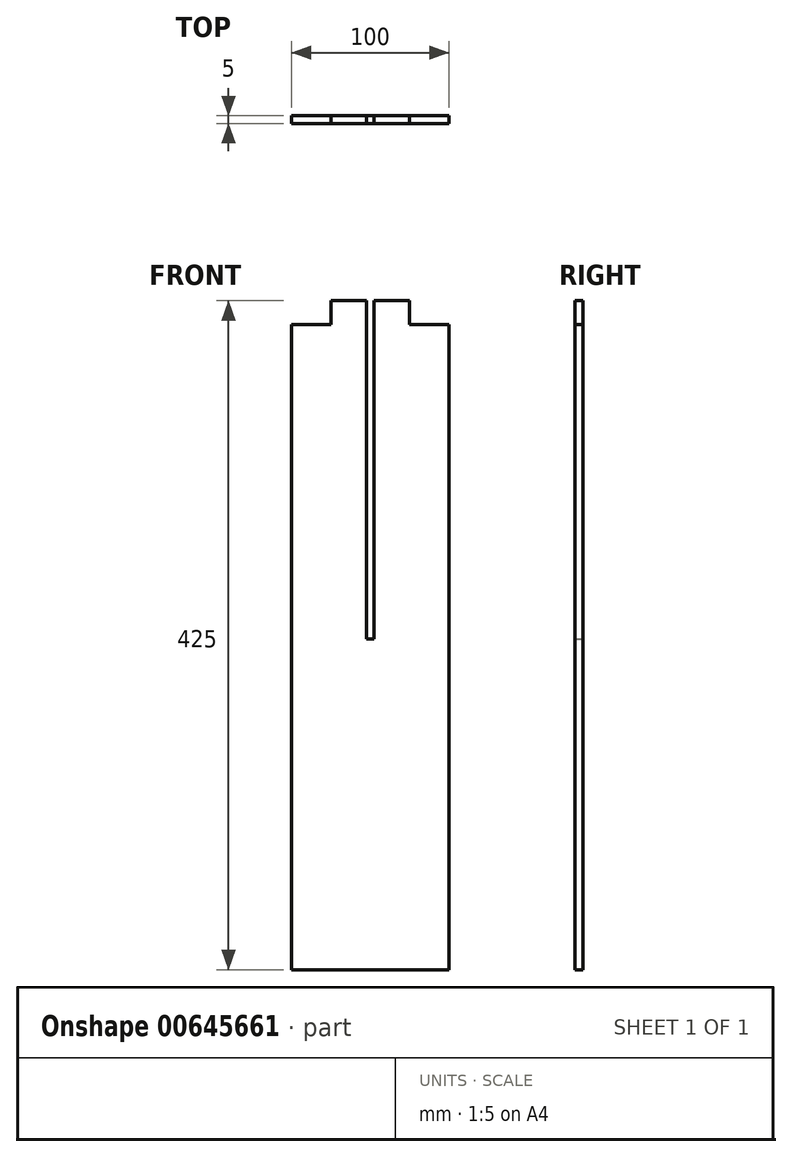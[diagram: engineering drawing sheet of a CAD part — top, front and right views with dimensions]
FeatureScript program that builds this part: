
annotation { "Feature Type Name" : "Feature", "Feature Type Description" : "" }
export const myFeature = defineFeature(function(context is Context, id is Id, definition is map)
    precondition{}
    {
        {
            var Q0;
            Q0=qCreatedBy(makeId("Front.planeOp"),FACE);
            var sketch = newSketch(context, id + "F0", { "sketchPlane" : qUnion([Q0])});
            skLineSegment(sketch, "E0.bottom", {"start": v(0, 0) * mm, "end": v(-100, 0) * mm});
            skLineSegment(sketch, "E0.left", {"start": v(0, 0) * mm, "end": v(0, 410) * mm});
            skLineSegment(sketch, "E0.right", {"start": v(-100, 0) * mm, "end": v(-100, 410) * mm});
            skLineSegment(sketch, "E1", {"start": v(-100, 410) * mm, "end": v(-75, 410) * mm});
            skLineSegment(sketch, "E2", {"start": v(-25, 410) * mm, "end": v(0, 410) * mm});
            skLineSegment(sketch, "E3.left", {"start": v(-52.5, 410) * mm, "end": v(-52.5, 410) * mm});
            skLineSegment(sketch, "E3.right", {"start": v(-47.5, 410) * mm, "end": v(-47.5, 410) * mm});
            skLineSegment(sketch, "E4.bottom", {"start": v(-52.5, 210) * mm, "end": v(-47.5, 210) * mm});
            skLineSegment(sketch, "E4.left", {"start": v(-52.5, 210) * mm, "end": v(-52.5, 410) * mm});
            skLineSegment(sketch, "E4.right", {"start": v(-47.5, 210) * mm, "end": v(-47.5, 410) * mm});
            skLineSegment(sketch, "E5.top", {"start": v(-47.5, 425) * mm, "end": v(-25, 425) * mm});
            skLineSegment(sketch, "E5.left", {"start": v(-47.5, 410) * mm, "end": v(-47.5, 425) * mm});
            skLineSegment(sketch, "E5.right", {"start": v(-25, 410) * mm, "end": v(-25, 425) * mm});
            skLineSegment(sketch, "E6.top", {"start": v(-52.5, 425) * mm, "end": v(-75, 425) * mm});
            skLineSegment(sketch, "E6.left", {"start": v(-52.5, 410) * mm, "end": v(-52.5, 425) * mm});
            skLineSegment(sketch, "E6.right", {"start": v(-75, 410) * mm, "end": v(-75, 425) * mm});
            skSolve(sketch);
        }
        {
            var Q0;
            Q0=makeQuery(id+"F0.imprint","IMPRINT",FACE,{"disambiguationData":[TD([[makeQuery(id+"F0.imprint","IMPRINT",EDGE,{"derivedFrom":sQuery(id+"F0.wireOp",EDGE,"E0.bottom")}),-1.0]])]});
            extrude(context, id + "F1", {"entities" : qUnion([Q0]), "depth" : 5 * mm, "offsetDistance" : 25 * mm});
        }
    });
